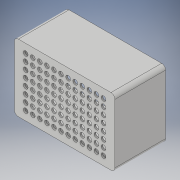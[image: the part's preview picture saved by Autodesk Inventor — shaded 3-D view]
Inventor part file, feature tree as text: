
AUTODESK INVENTOR PART (.ipt)
format: ipt  version: 2019.4 (Build 234330000, 330)  size: 249,344 bytes
history: native  units: mm
features: reference x5, extrude x3, sketch x2, other x2, fillet x1, pattern_linear x1, projected_geometry x1
ambient origin geometry x8: Origin, YZ Plane, XZ Plane, XY Plane, X Axis, Y Axis, Z Axis, Center Point
bodies: Solid1 (feature_tree)
feature tree (15):
  extrude  "Extrusion1"  Depth=5.0mm
  fillet  "Fillet1"  Radius=2.0mm
  extrude  "Extrusion2"  Depth=127.76mm
  extrude  "Extrusion3"  Depth=85.48mm
  pattern_linear  "Rectangular Pattern1"  Spacing1=6.0mm  [1 undecoded]
  sketch  "Sketch1"  dims[d0=2.0mm d1=0.0mm d2=5.0mm d13=2.0mm d14=0.0mm]
  reference  "Reference1"
  reference  "Reference2"
  reference  "Reference3"
  reference  "Reference4"
  reference  "Reference5"
  sketch  "Sketch2"  dims[d28=62.49mm d29=0.0mm d30=127.76mm d31=85.48mm d35=6.0mm d36=14.38mm d37=11.24mm d38=120.0mm d40=9.0mm d41=80.0mm d43=9.0mm]
  projected_geometry  "Projected Loop2"
  other  "Assembly1"
  other  "00_MTP_96-welplate:1"
note: 1 required parameter value undecoded (feature->parameter linkage not recoverable at this tier; creation-order binding heuristic only, values carry confidence <= 0.55)
